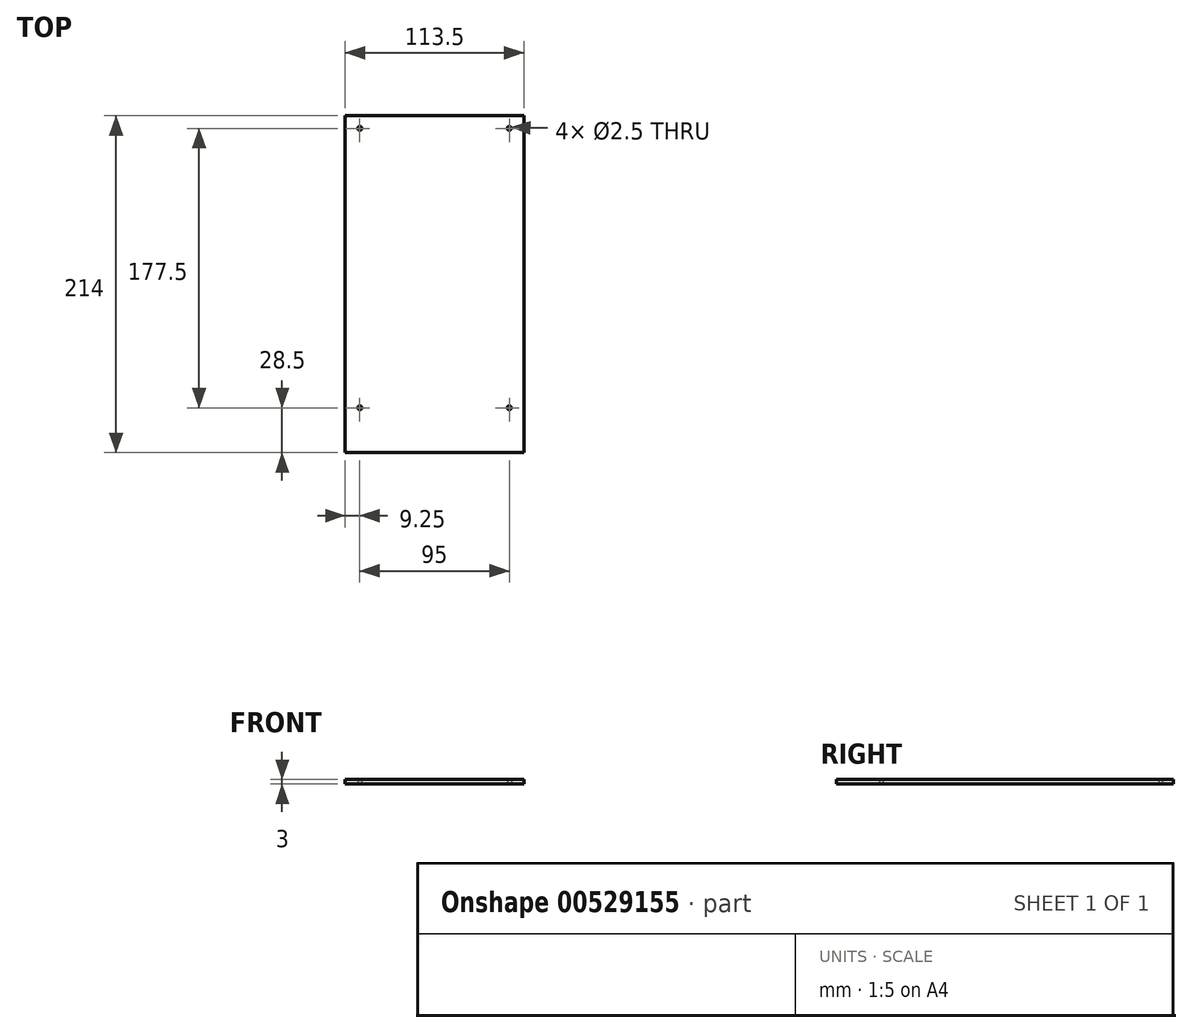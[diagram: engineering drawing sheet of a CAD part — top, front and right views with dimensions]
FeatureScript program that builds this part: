
annotation { "Feature Type Name" : "Feature", "Feature Type Description" : "" }
export const myFeature = defineFeature(function(context is Context, id is Id, definition is map)
    precondition{}
    {
        {
            var Q0;
            Q0=qCreatedBy(makeId("Top.planeOp"),FACE);
            var sketch = newSketch(context, id + "F0", { "sketchPlane" : qUnion([Q0])});
            skLineSegment(sketch, "E0.bottom", {"start": v(-56.75, 107) * mm, "end": v(56.75, 107) * mm});
            skLineSegment(sketch, "E0.top", {"start": v(-56.75, -107) * mm, "end": v(56.75, -107) * mm});
            skLineSegment(sketch, "E0.left", {"start": v(-56.75, 107) * mm, "end": v(-56.75, -107) * mm});
            skLineSegment(sketch, "E0.right", {"start": v(56.75, 107) * mm, "end": v(56.75, -107) * mm});
            skLineSegment(sketch, "E1", {"start": v(0, 120.85) * mm, "end": v(0, -119.58) * mm, "construction": true});
            skPoint(sketch, "E1.startSnap0", {"position": v(0, 107) * mm});
            skLineSegment(sketch, "E2", {"start": v(-70.8, 0) * mm, "end": v(72.17, 0) * mm, "construction": true});
            skPoint(sketch, "E2.startSnap0", {"position": v(-56.75, 0) * mm});
            skPoint(sketch, "E2.endSnap0", {"position": v(56.75, 0) * mm});
            skLineSegment(sketch, "E3", {"start": v(-61.75, 99) * mm, "end": v(62.58, 99) * mm, "construction": true});
            skLineSegment(sketch, "E4", {"start": v(-48.75, 111.96) * mm, "end": v(-48.75, -116.62) * mm, "construction": true});
            skLineSegment(sketch, "E5.MirrorCS", {"start": v(48.75, 111.96) * mm, "end": v(48.75, -116.62) * mm, "construction": true});
            skLineSegment(sketch, "E6.MirrorCS", {"start": v(-61.75, -99) * mm, "end": v(62.58, -99) * mm, "construction": true});
            skLineSegment(sketch, "E7", {"start": v(-46.25, 100.92) * mm, "end": v(-46.25, 97.12) * mm, "construction": true});
            skLineSegment(sketch, "E8.MirrorCS", {"start": v(46.25, 100.92) * mm, "end": v(46.25, 97.12) * mm, "construction": true});
            skCircle(sketch, "E9.MirrorC", {"center": v(47.5, 99) * mm, "radius": 1.25 * mm});
            skCircle(sketch, "E10.MirrorC", {"center": v(-47.5, 99) * mm, "radius": 1.25 * mm});
            skLineSegment(sketch, "E11", {"start": v(-47.5, 97.75) * mm, "end": v(-50.16, 97.75) * mm, "construction": true});
            skLineSegment(sketch, "E12", {"start": v(-50.16, 97.75) * mm, "end": v(-45.26, 97.75) * mm, "construction": true});
            skLineSegment(sketch, "E13", {"start": v(-65.42, -77.25) * mm, "end": v(67.2, -77.25) * mm, "construction": true});
            skLineSegment(sketch, "E14", {"start": v(-66.1, 10.25) * mm, "end": v(71.33, 10.25) * mm, "construction": true});
            skCircle(sketch, "E15.MirrorC", {"center": v(-47.5, -78.5) * mm, "radius": 1.25 * mm});
            skCircle(sketch, "E16.MirrorC", {"center": v(47.5, -78.5) * mm, "radius": 1.25 * mm});
            skSolve(sketch);
        }
        {
            var Q0;
            Q0=makeQuery(id+"F0.imprint","IMPRINT",FACE,{"disambiguationData":[TD([[makeQuery(id+"F0.imprint","IMPRINT",EDGE,{"derivedFrom":sQuery(id+"F0.wireOp",EDGE,"E0.bottom")}),-1.0]])]});
            extrude(context, id + "F1", {"entities" : qUnion([Q0]), "depth" : 3 * mm, "offsetDistance" : 25 * mm});
        }
    });
